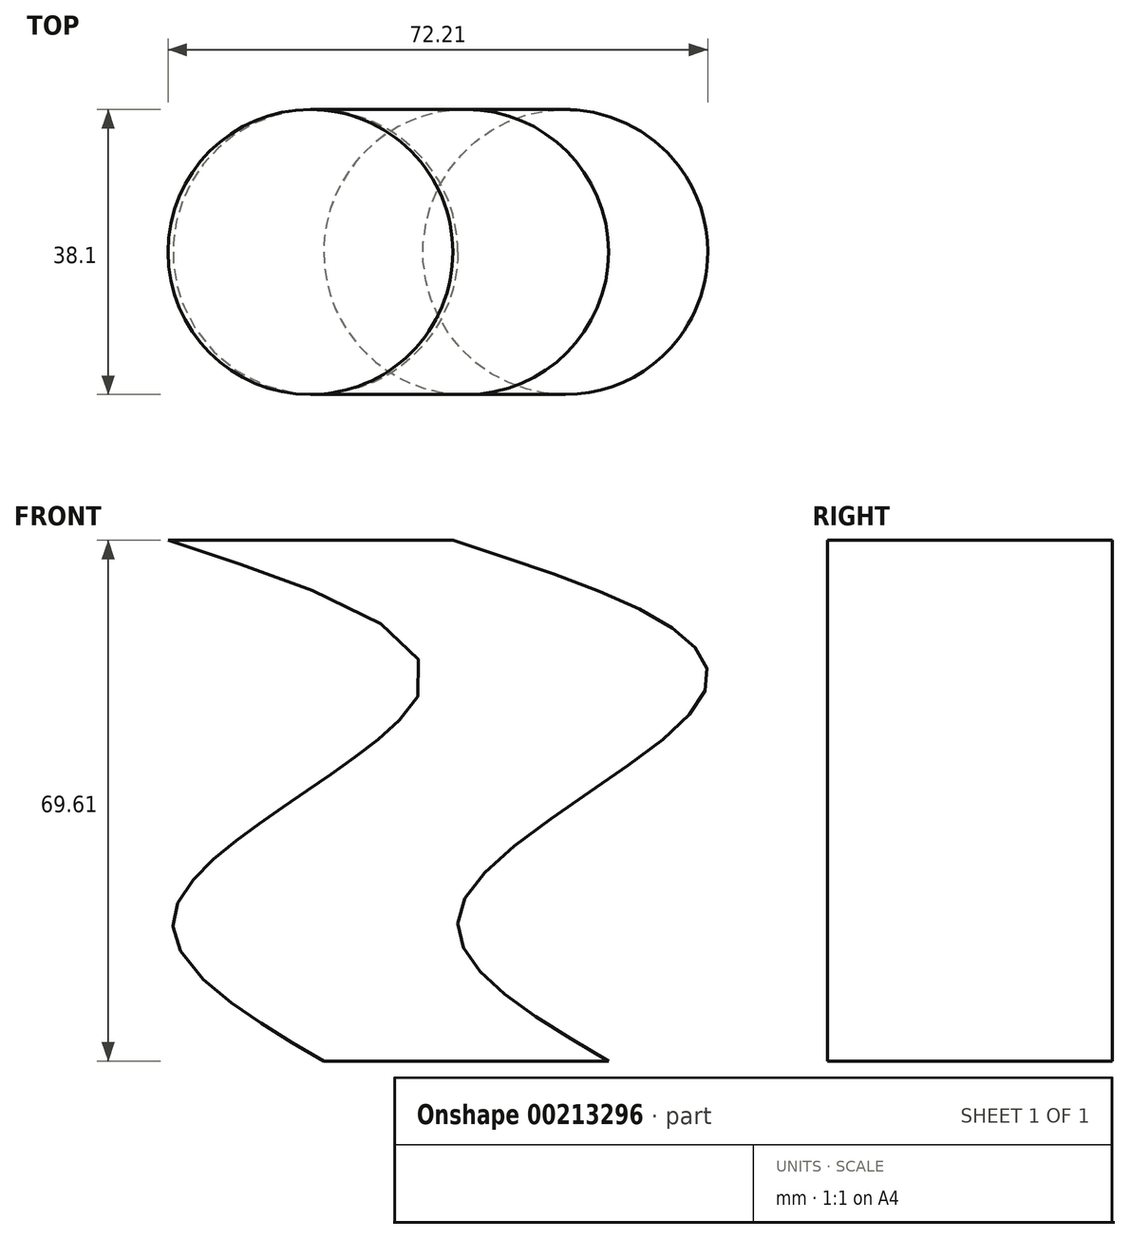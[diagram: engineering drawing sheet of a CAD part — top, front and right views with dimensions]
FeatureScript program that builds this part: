
annotation { "Feature Type Name" : "Feature", "Feature Type Description" : "" }
export const myFeature = defineFeature(function(context is Context, id is Id, definition is map)
    precondition{}
    {
        {
            var Q0;
            Q0=qCreatedBy(makeId("Top.planeOp"),FACE);
            var sketch = newSketch(context, id + "F0", { "sketchPlane" : qUnion([Q0])});
            skCircle(sketch, "E0", {"center": v(0, 0) * mm, "radius": 19.05 * mm});
            skSolve(sketch);
        }
        {
            var Q0;
            Q0=qCreatedBy(makeId("Front.planeOp"),FACE);
            var sketch = newSketch(context, id + "F1", { "sketchPlane" : qUnion([Q0])});
            skFitSpline(sketch, "E1", {"points": [v(-1.8, 0) * mm, v(-21.43, 20.93) * mm, v(11.22, 49.78) * mm, v(-22.63, 69.6) * mm], "startDerivative": vector(-116.26, 67.8) * mm, "endDerivative": vector(-159.24, 51.33) * mm});
            skSolve(sketch);
        }
        {
            var Q0;
            Q0=makeQuery(id+"F0.imprint","IMPRINT",FACE,{"disambiguationData":[TD([[makeQuery(id+"F0.imprint","IMPRINT",EDGE,{"derivedFrom":sQuery(id+"F0.wireOp",EDGE,"E0")}),1.0]])]});
            var Q1;
            Q1=sQuery(id+"F1.wireOp",EDGE,"E1");
            sweep(context, id + "F2", {"profiles" : qUnion([Q0]), "path" : qUnion([Q1]), "keepProfileOrientation" : true});
        }
    });
